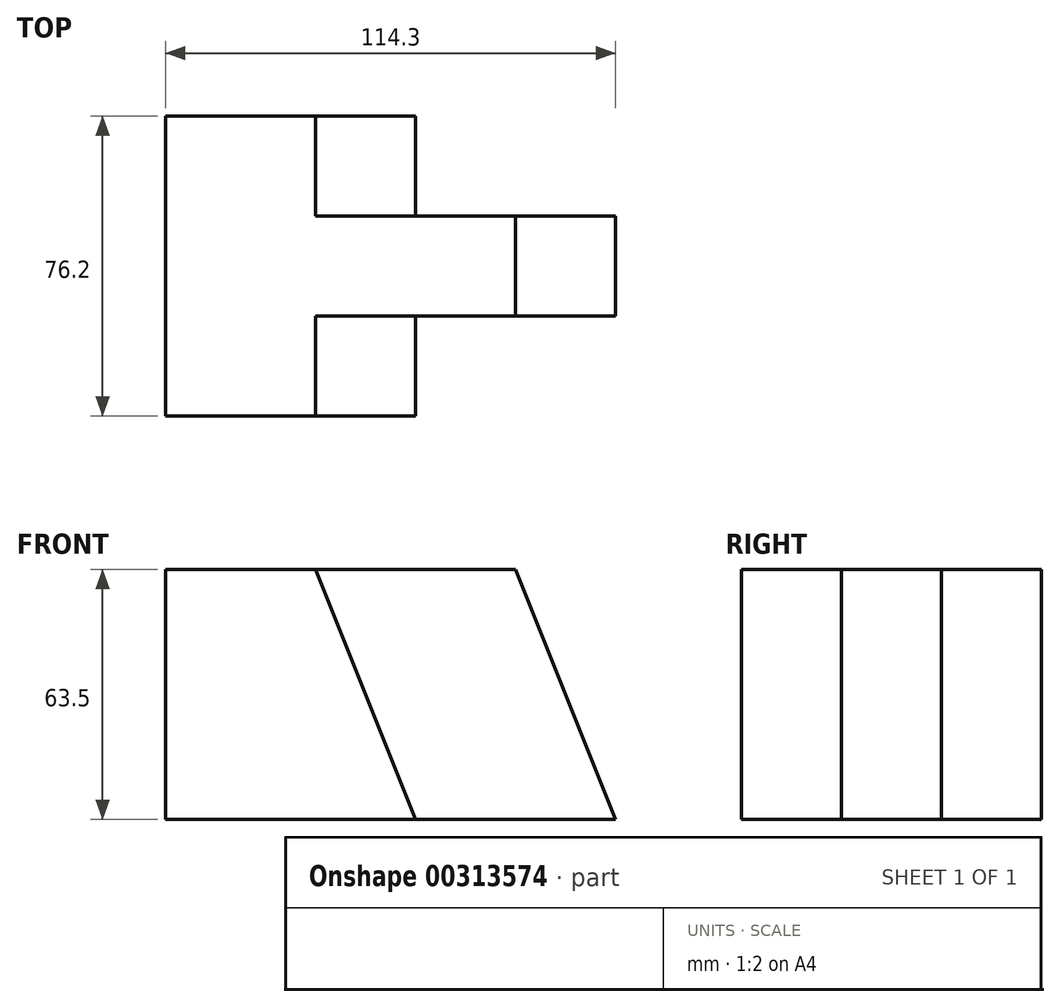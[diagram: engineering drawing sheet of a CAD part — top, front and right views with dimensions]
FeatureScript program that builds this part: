
annotation { "Feature Type Name" : "Feature", "Feature Type Description" : "" }
export const myFeature = defineFeature(function(context is Context, id is Id, definition is map)
    precondition{}
    {
        {
            var Q0;
            Q0=qCreatedBy(makeId("Front.planeOp"),FACE);
            var sketch = newSketch(context, id + "F0", { "sketchPlane" : qUnion([Q0])});
            skLineSegment(sketch, "E0", {"start": v(-19.05, 31.75) * mm, "end": v(-57.15, 31.75) * mm});
            skLineSegment(sketch, "E1", {"start": v(-57.15, 31.75) * mm, "end": v(-57.15, -31.75) * mm});
            skLineSegment(sketch, "E2", {"start": v(-57.15, -31.75) * mm, "end": v(6.35, -31.75) * mm});
            skLineSegment(sketch, "E3", {"start": v(6.35, -31.75) * mm, "end": v(-19.05, 31.75) * mm});
            skLineSegment(sketch, "E4", {"start": v(-19.05, 31.75) * mm, "end": v(31.75, 31.75) * mm});
            skLineSegment(sketch, "E5", {"start": v(31.75, 31.75) * mm, "end": v(57.15, -31.75) * mm});
            skLineSegment(sketch, "E6", {"start": v(57.15, -31.75) * mm, "end": v(6.35, -31.75) * mm});
            skSolve(sketch);
        }
        {
            var Q0;
            Q0=makeQuery(id+"F0.imprint","IMPRINT",FACE,{"disambiguationData":[TD([[makeQuery(id+"F0.imprint","IMPRINT",EDGE,{"derivedFrom":sQuery(id+"F0.wireOp",EDGE,"E0")}),1.0]])]});
            extrude(context, id + "F1", {"entities" : qUnion([Q0]), "endBound" : BoundingType.SYMMETRIC, "depth" : 76.2 * mm});
        }
        {
            var Q0;
            Q0=makeQuery(id+"F0.imprint","IMPRINT",FACE,{"disambiguationData":[TD([[makeQuery(id+"F0.imprint","IMPRINT",EDGE,{"derivedFrom":sQuery(id+"F0.wireOp",EDGE,"E3")}),-1.0]])]});
            var Q1;
            Q1=makeQuery(id+"F0.imprint","IMPRINT",FACE,{"disambiguationData":[TD([[makeQuery(id+"F0.imprint","IMPRINT",EDGE,{"derivedFrom":sQuery(id+"F0.wireOp",EDGE,"E0")}),1.0]])]});
            extrude(context, id + "F2", {"entities" : qUnion([Q0, Q1]), "operationType" : NewBodyOperationType.ADD, "endBound" : BoundingType.SYMMETRIC, "depth" : 25.4 * mm});
        }
    });
